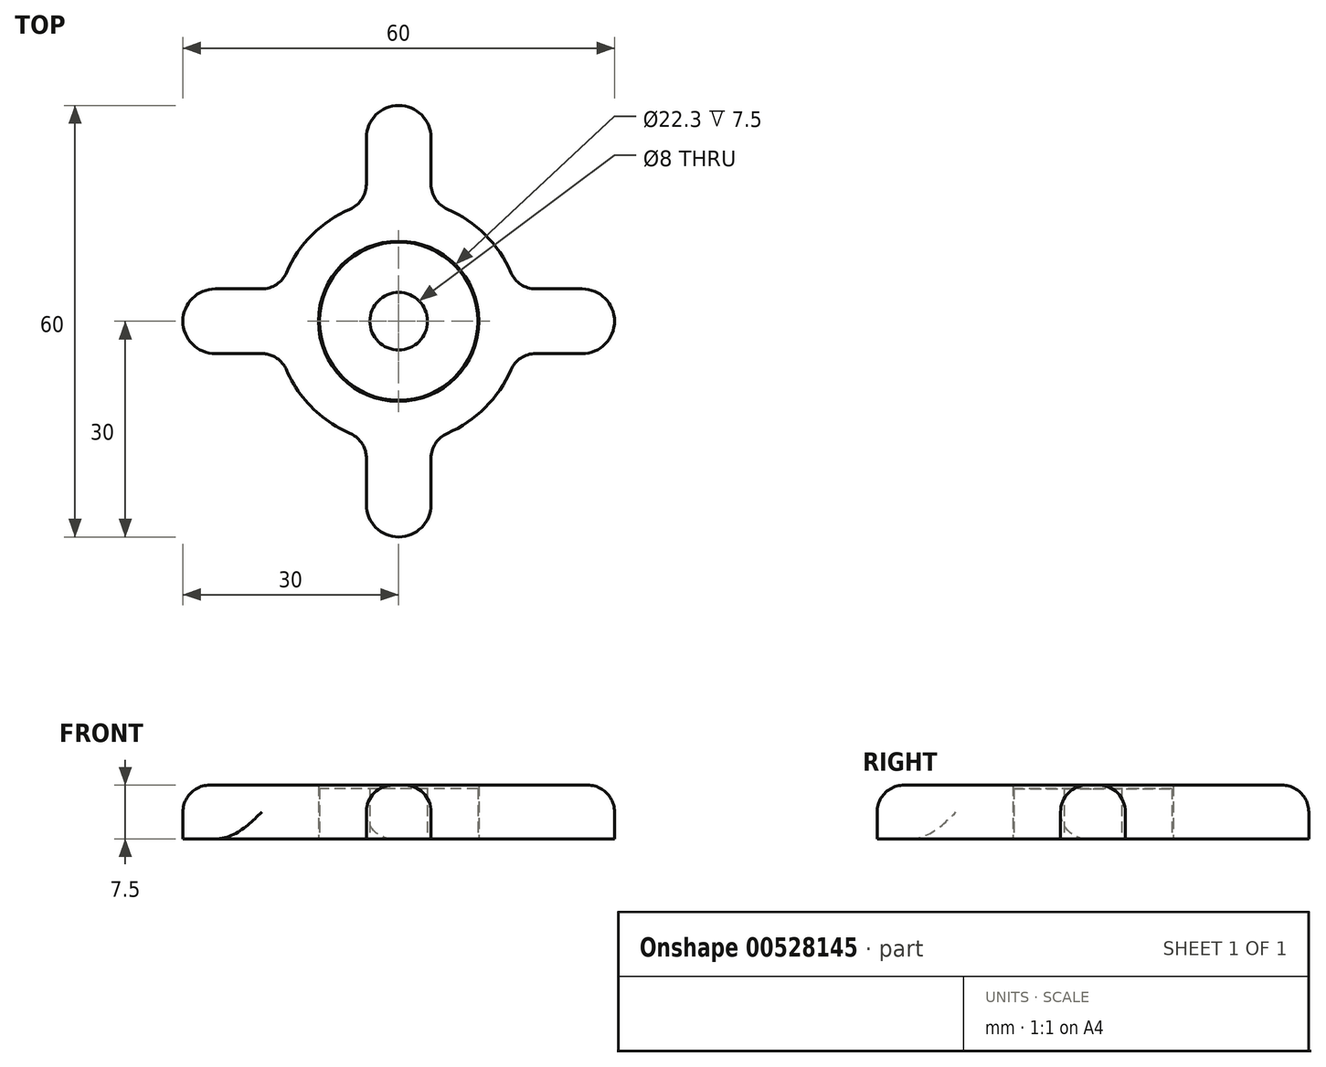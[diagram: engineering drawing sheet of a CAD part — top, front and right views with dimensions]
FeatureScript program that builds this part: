
annotation { "Feature Type Name" : "Feature", "Feature Type Description" : "" }
export const myFeature = defineFeature(function(context is Context, id is Id, definition is map)
    precondition{}
    {
        {
            var Q0;
            Q0=qCreatedBy(makeId("Top.planeOp"),FACE);
            var sketch = newSketch(context, id + "F0", { "sketchPlane" : qUnion([Q0])});
            skCircle(sketch, "E0", {"center": v(0, 0) * mm, "radius": 4 * mm});
            skCircle(sketch, "E1", {"center": v(0, 0) * mm, "radius": 11 * mm});
            skSolve(sketch);
        }
        {
            var Q0;
            Q0=makeQuery(id+"F0.imprint","IMPRINT",FACE,{"disambiguationData":[TD([[makeQuery(id+"F0.imprint","IMPRINT",EDGE,{"derivedFrom":sQuery(id+"F0.wireOp",EDGE,"E0")}),-1.0]])]});
            extrude(context, id + "F1", {"entities" : qUnion([Q0]), "depth" : 7 * mm, "offsetDistance" : 25 * mm});
        }
        {
            var Q0;
            Q0=qCreatedBy(makeId("Top.planeOp"),FACE);
            var sketch = newSketch(context, id + "F2", { "sketchPlane" : qUnion([Q0])});
            skLineSegment(sketch, "E2.bottom", {"start": v(0, 30) * mm, "end": v(0, 30) * mm});
            skLineSegment(sketch, "E2.top", {"start": v(0, -30) * mm, "end": v(0, -30) * mm});
            skLineSegment(sketch, "E2.left", {"start": v(4.5, 25.5) * mm, "end": v(4.5, 16.4) * mm});
            skLineSegment(sketch, "E2.right", {"start": v(-4.5, 25.5) * mm, "end": v(-4.5, 16.4) * mm});
            skPoint(sketch, "E2.middle", {"position": v(0, 0) * mm});
            skLineSegment(sketch, "E3.bottom", {"start": v(-25.5, 4.5) * mm, "end": v(-16.4, 4.5) * mm});
            skLineSegment(sketch, "E3.top", {"start": v(-25.5, -4.5) * mm, "end": v(-16.4, -4.5) * mm});
            skLineSegment(sketch, "E3.left", {"start": v(-30, 0) * mm, "end": v(-30, 0) * mm});
            skLineSegment(sketch, "E3.right", {"start": v(30, 0) * mm, "end": v(30, 0) * mm});
            skPoint(sketch, "E4.visualSharp", {"position": v(-30, 4.5) * mm});
            skArc(sketch, "E4.filletArc", {"start": v(-25.5, 4.5) * mm, "mid": v(-28.68, 3.18) * mm, "end": v(-30, 0) * mm});
            skPoint(sketch, "E5.visualSharp", {"position": v(-30, -4.5) * mm});
            skArc(sketch, "E5.filletArc", {"start": v(-30, 0) * mm, "mid": v(-28.68, -3.18) * mm, "end": v(-25.5, -4.5) * mm});
            skPoint(sketch, "E6.visualSharp", {"position": v(-4.5, 30) * mm});
            skArc(sketch, "E6.filletArc", {"start": v(0, 30) * mm, "mid": v(-3.18, 28.68) * mm, "end": v(-4.5, 25.5) * mm});
            skPoint(sketch, "E7.visualSharp", {"position": v(4.5, 30) * mm});
            skArc(sketch, "E7.filletArc", {"start": v(4.5, 25.5) * mm, "mid": v(3.18, 28.68) * mm, "end": v(0, 30) * mm});
            skPoint(sketch, "E8.visualSharp", {"position": v(4.5, -30) * mm});
            skArc(sketch, "E8.filletArc", {"start": v(0, -30) * mm, "mid": v(3.18, -28.68) * mm, "end": v(4.5, -25.5) * mm});
            skPoint(sketch, "E9.visualSharp", {"position": v(-4.5, -30) * mm});
            skArc(sketch, "E9.filletArc", {"start": v(-4.5, -25.5) * mm, "mid": v(-3.18, -28.68) * mm, "end": v(0, -30) * mm});
            skPoint(sketch, "E10.visualSharp", {"position": v(30, 4.5) * mm});
            skArc(sketch, "E10.filletArc", {"start": v(30, 0) * mm, "mid": v(28.68, 3.18) * mm, "end": v(25.5, 4.5) * mm});
            skPoint(sketch, "E11.visualSharp", {"position": v(30, -4.5) * mm});
            skArc(sketch, "E11.filletArc", {"start": v(25.5, -4.5) * mm, "mid": v(28.68, -3.18) * mm, "end": v(30, 0) * mm});
            skArc(sketch, "E12.0", {"start": v(-4.5, 16.4) * mm, "mid": v(-12.02, 12.02) * mm, "end": v(-16.4, 4.5) * mm});
            skCircle(sketch, "E13.0", {"center": v(0, 0) * mm, "radius": 11.15 * mm});
            skLineSegment(sketch, "E14.trimOffspring", {"start": v(16.4, 4.5) * mm, "end": v(25.5, 4.5) * mm});
            skLineSegment(sketch, "E15.trimOffspring", {"start": v(16.4, -4.5) * mm, "end": v(25.5, -4.5) * mm});
            skLineSegment(sketch, "E16.trimOffspring", {"start": v(4.5, -16.4) * mm, "end": v(4.5, -25.5) * mm});
            skArc(sketch, "E17.trimOffspring", {"start": v(16.4, 4.5) * mm, "mid": v(12.02, 12.02) * mm, "end": v(4.5, 16.4) * mm});
            skArc(sketch, "E18.trimOffspring", {"start": v(4.5, -16.4) * mm, "mid": v(12.02, -12.02) * mm, "end": v(16.4, -4.5) * mm});
            skLineSegment(sketch, "E19.trimOffspring", {"start": v(-4.5, -16.4) * mm, "end": v(-4.5, -25.5) * mm});
            skArc(sketch, "E20.trimOffspring", {"start": v(-16.4, -4.5) * mm, "mid": v(-12.02, -12.02) * mm, "end": v(-4.5, -16.4) * mm});
            skSolve(sketch);
        }
        {
            var Q0;
            Q0=makeQuery(id+"F2.imprint","IMPRINT",FACE,{"disambiguationData":[TD([[makeQuery(id+"F2.imprint","IMPRINT",EDGE,{"derivedFrom":sQuery(id+"F2.wireOp",EDGE,"E2.left")}),-1.0]])]});
            extrude(context, id + "F3", {"entities" : qUnion([Q0]), "depth" : 7.5 * mm, "offsetDistance" : 25 * mm});
        }
        {
            var Q0;
            Q0=makeQuery(id+"F3.opExtrude","CAP_EDGE",EDGE,{"disambiguationData":[OSD([sQuery(id+"F2.wireOp",EDGE,"E3.top")])],"isStart":false});
            var Q1;
            Q1=makeQuery(id+"F3.opExtrude","CAP_EDGE",EDGE,{"disambiguationData":[OSD([sQuery(id+"F2.wireOp",EDGE,"E20.trimOffspring")])],"isStart":true});
            var Q2;
            Q2=makeQuery(id+"F3.opExtrude","CAP_EDGE",EDGE,{"disambiguationData":[OSD([sQuery(id+"F2.wireOp",EDGE,"E19.trimOffspring")])],"isStart":false});
            var Q3;
            Q3=makeQuery(id+"F3.opExtrude","CAP_EDGE",EDGE,{"disambiguationData":[OSD([sQuery(id+"F2.wireOp",EDGE,"E18.trimOffspring")])],"isStart":false});
            var Q4;
            Q4=makeQuery(id+"F3.opExtrude","CAP_EDGE",EDGE,{"disambiguationData":[OSD([sQuery(id+"F2.wireOp",EDGE,"E15.trimOffspring")])],"isStart":false});
            var Q5;
            Q5=makeQuery(id+"F3.opExtrude","CAP_EDGE",EDGE,{"disambiguationData":[OSD([sQuery(id+"F2.wireOp",EDGE,"E2.left")])],"isStart":false});
            var Q6;
            Q6=makeQuery(id+"F3.opExtrude","CAP_EDGE",EDGE,{"disambiguationData":[OSD([sQuery(id+"F2.wireOp",EDGE,"E20.trimOffspring")])],"isStart":false});
            var Q7;
            Q7=makeQuery(id+"F3.opExtrude","CAP_EDGE",EDGE,{"disambiguationData":[OSD([sQuery(id+"F2.wireOp",EDGE,"E12.0")])],"isStart":false});
            var Q8;
            Q8=makeQuery(id+"F3.opExtrude","CAP_EDGE",EDGE,{"disambiguationData":[OSD([sQuery(id+"F2.wireOp",EDGE,"E17.trimOffspring")])],"isStart":false});
            var Q9;
            Q9=makeQuery(id+"F3.opExtrude","SWEPT_EDGE",EDGE,{"disambiguationData":[OSD([sQuery(id+"F2.wireOp",EDGE,"E2.left"),sQuery(id+"F2.wireOp",EDGE,"E17.trimOffspring")])]});
            var Q10;
            Q10=makeQuery(id+"F3.opExtrude","SWEPT_EDGE",EDGE,{"disambiguationData":[OSD([sQuery(id+"F2.wireOp",EDGE,"E14.trimOffspring"),sQuery(id+"F2.wireOp",EDGE,"E17.trimOffspring")])]});
            var Q11;
            Q11=makeQuery(id+"F3.opExtrude","SWEPT_EDGE",EDGE,{"disambiguationData":[OSD([sQuery(id+"F2.wireOp",EDGE,"E3.bottom"),sQuery(id+"F2.wireOp",EDGE,"E12.0")])]});
            var Q12;
            Q12=makeQuery(id+"F3.opExtrude","SWEPT_EDGE",EDGE,{"disambiguationData":[OSD([sQuery(id+"F2.wireOp",EDGE,"E2.right"),sQuery(id+"F2.wireOp",EDGE,"E12.0")])]});
            var Q13;
            Q13=makeQuery(id+"F3.opExtrude","SWEPT_EDGE",EDGE,{"disambiguationData":[OSD([sQuery(id+"F2.wireOp",EDGE,"E19.trimOffspring"),sQuery(id+"F2.wireOp",EDGE,"E20.trimOffspring")])]});
            var Q14;
            Q14=makeQuery(id+"F3.opExtrude","SWEPT_EDGE",EDGE,{"disambiguationData":[OSD([sQuery(id+"F2.wireOp",EDGE,"E3.top"),sQuery(id+"F2.wireOp",EDGE,"E20.trimOffspring")])]});
            var Q15;
            Q15=makeQuery(id+"F3.opExtrude","SWEPT_EDGE",EDGE,{"disambiguationData":[OSD([sQuery(id+"F2.wireOp",EDGE,"E15.trimOffspring"),sQuery(id+"F2.wireOp",EDGE,"E18.trimOffspring")])]});
            var Q16;
            Q16=makeQuery(id+"F3.opExtrude","SWEPT_EDGE",EDGE,{"disambiguationData":[OSD([sQuery(id+"F2.wireOp",EDGE,"E16.trimOffspring"),sQuery(id+"F2.wireOp",EDGE,"E18.trimOffspring")])]});
            fillet(context, id + "F4", {"entities" : qUnion([Q0, Q1, Q2, Q3, Q4, Q5, Q6, Q7, Q8, Q9, Q10, Q11, Q12, Q13, Q14, Q15, Q16]), "radius" : 3.75 * mm, "tangentPropagation" : true, "allowEdgeOverflow" : false});
        }
    });
